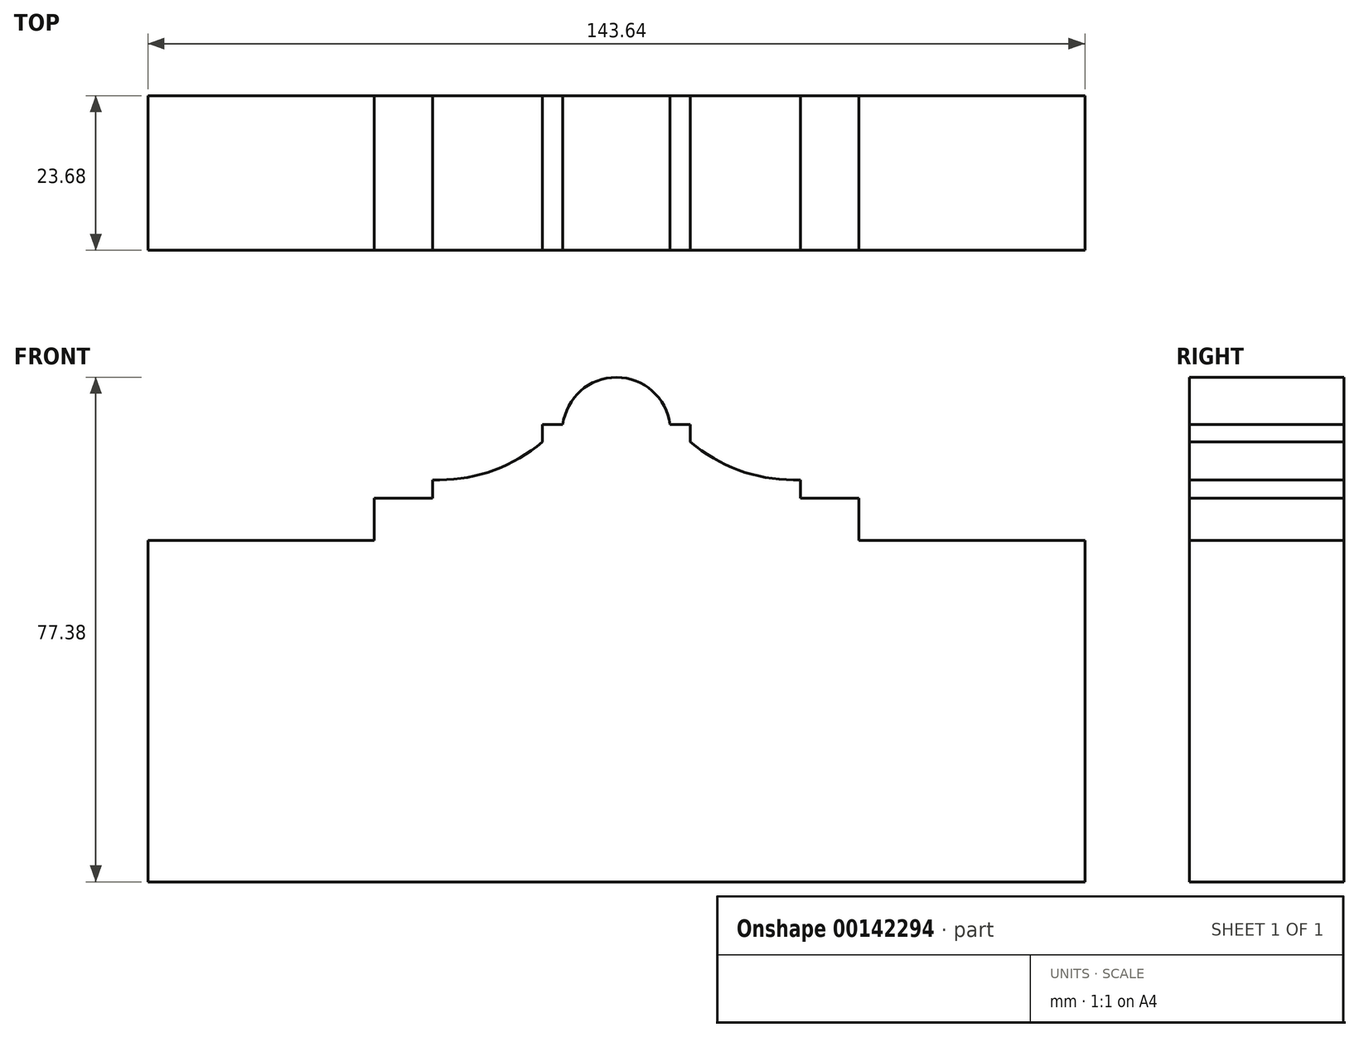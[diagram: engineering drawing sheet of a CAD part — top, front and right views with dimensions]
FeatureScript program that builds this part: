
annotation { "Feature Type Name" : "Feature", "Feature Type Description" : "" }
export const myFeature = defineFeature(function(context is Context, id is Id, definition is map)
    precondition{}
    {
        {
            var Q0;
            Q0=qCreatedBy(makeId("Front.planeOp"),FACE);
            var sketch = newSketch(context, id + "F0", { "sketchPlane" : qUnion([Q0])});
            skLineSegment(sketch, "E0", {"start": v(-71.82, 0) * mm, "end": v(-71.82, 52.38) * mm});
            skLineSegment(sketch, "E1", {"start": v(-71.82, 52.38) * mm, "end": v(-37.15, 52.38) * mm});
            skLineSegment(sketch, "E2", {"start": v(-37.15, 52.38) * mm, "end": v(-37.15, 58.8) * mm});
            skLineSegment(sketch, "E3", {"start": v(-37.15, 58.8) * mm, "end": v(-28.19, 58.8) * mm});
            skLineSegment(sketch, "E4", {"start": v(-28.19, 58.8) * mm, "end": v(-28.19, 61.64) * mm});
            skLineSegment(sketch, "E5", {"start": v(-11.34, 67.48) * mm, "end": v(-11.34, 70.11) * mm});
            skLineSegment(sketch, "E6", {"start": v(-11.34, 70.11) * mm, "end": v(-8.21, 70.11) * mm});
            skLineSegment(sketch, "E7", {"start": v(-28.19, 61.64) * mm, "end": v(-27.12, 61.64) * mm});
            skArc(sketch, "E8", {"start": v(-27.12, 61.64) * mm, "mid": v(-18.71, 63.15) * mm, "end": v(-11.34, 67.48) * mm});
            skLineSegment(sketch, "E9", {"start": v(-71.82, 0) * mm, "end": v(0, 0) * mm});
            skLineSegment(sketch, "E10", {"start": v(0, 0) * mm, "end": v(0, 77.38) * mm});
            skArc(sketch, "E11", {"start": v(0, 77.38) * mm, "mid": v(-5.48, 75.3) * mm, "end": v(-8.21, 70.11) * mm});
            skSolve(sketch);
        }
        {
            var Q0;
            Q0=makeQuery(id+"F0.imprint","IMPRINT",FACE,{"disambiguationData":[TD([[makeQuery(id+"F0.imprint","IMPRINT",EDGE,{"derivedFrom":sQuery(id+"F0.wireOp",EDGE,"E0")}),-1.0]])]});
            extrude(context, id + "F1", {"entities" : qUnion([Q0]), "oppositeDirection" : true, "depth" : 23.68 * mm});
        }
        {
            var Q0;
            Q0=makeQuery(id+"F1.opExtrude","SWEPT_BODY",BODY,{"disambiguationData":[OSD([sQuery(id+"F0.wireOp",EDGE,"E0"),sQuery(id+"F0.wireOp",EDGE,"E1"),sQuery(id+"F0.wireOp",EDGE,"E2"),sQuery(id+"F0.wireOp",EDGE,"E3"),sQuery(id+"F0.wireOp",EDGE,"E4"),sQuery(id+"F0.wireOp",EDGE,"E5"),sQuery(id+"F0.wireOp",EDGE,"E6"),sQuery(id+"F0.wireOp",EDGE,"E7"),sQuery(id+"F0.wireOp",EDGE,"E8"),sQuery(id+"F0.wireOp",EDGE,"E9"),sQuery(id+"F0.wireOp",EDGE,"E10"),sQuery(id+"F0.wireOp",EDGE,"E11")])]});
            var Q1;
            Q1=qCreatedBy(makeId("Right.planeOp"),FACE);
            mirror(context, id + "F2", {"operationType" : NewBodyOperationType.ADD, "entities" : qUnion([Q0]), "mirrorPlane" : qUnion([Q1])});
        }
    });
